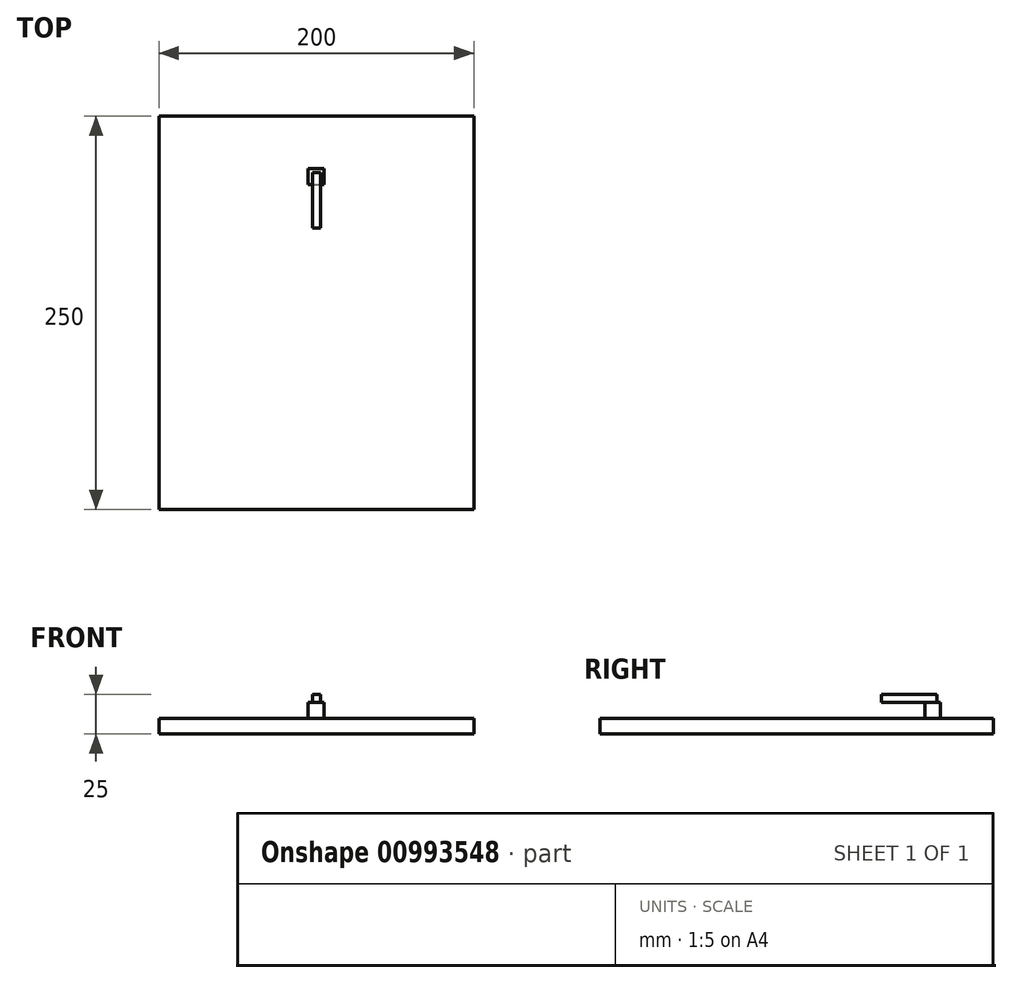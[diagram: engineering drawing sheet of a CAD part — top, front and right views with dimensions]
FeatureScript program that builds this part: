
annotation { "Feature Type Name" : "Feature", "Feature Type Description" : "" }
export const myFeature = defineFeature(function(context is Context, id is Id, definition is map)
    precondition{}
    {
        {
            var Q0;
            Q0=qCreatedBy(makeId("Top.planeOp"),FACE);
            var sketch = newSketch(context, id + "F0", { "sketchPlane" : qUnion([Q0])});
            skLineSegment(sketch, "E0.bottom", {"start": v(100, -125) * mm, "end": v(-100, -125) * mm});
            skLineSegment(sketch, "E0.top", {"start": v(100, 125) * mm, "end": v(-100, 125) * mm});
            skLineSegment(sketch, "E0.left", {"start": v(100, -125) * mm, "end": v(100, 125) * mm});
            skLineSegment(sketch, "E0.right", {"start": v(-100, -125) * mm, "end": v(-100, 125) * mm});
            skPoint(sketch, "E0.middle", {"position": v(0, 0) * mm});
            skSolve(sketch);
        }
        {
            var Q0;
            Q0 = qSketchRegion(id + "F0", true);
            extrude(context, id + "F1", {"entities" : qUnion([Q0]), "depth" : 10 * mm, "offsetDistance" : 25 * mm});
        }
        {
            var Q0;
            Q0=makeQuery(id+"F1.opExtrude","CAP_FACE",FACE,{"disambiguationData":[OSD([sQuery(id+"F0.wireOp",EDGE,"E0.bottom"),sQuery(id+"F0.wireOp",EDGE,"E0.top"),sQuery(id+"F0.wireOp",EDGE,"E0.left"),sQuery(id+"F0.wireOp",EDGE,"E0.right")])],"isStart":false});
            var sketch = newSketch(context, id + "F2", { "sketchPlane" : qUnion([Q0])});
            skLineSegment(sketch, "E1.bottom", {"start": v(-5.22, 91.46) * mm, "end": v(4.78, 91.46) * mm});
            skLineSegment(sketch, "E1.top", {"start": v(-5.22, 81.46) * mm, "end": v(4.78, 81.46) * mm});
            skLineSegment(sketch, "E1.left", {"start": v(-5.22, 91.46) * mm, "end": v(-5.22, 81.46) * mm});
            skLineSegment(sketch, "E1.right", {"start": v(4.78, 91.46) * mm, "end": v(4.78, 81.46) * mm});
            skLineSegment(sketch, "E2", {"start": v(0, 0) * mm, "end": v(0, 120.17) * mm});
            skSolve(sketch);
        }
        {
            var Q0;
            Q0 = qSketchRegion(id + "F2", true);
            extrude(context, id + "F3", {"entities" : qUnion([Q0]), "operationType" : NewBodyOperationType.ADD, "depth" : 10 * mm, "offsetDistance" : 25 * mm});
        }
        {
            var Q0;
            Q0=qCreatedBy(makeId("Top.planeOp"),FACE);
            cPlane(context, id + "F4", {"entities" : qUnion([Q0]), "cplaneType" : CPlaneType.OFFSET, "offset" : 20.1 * mm, "width" : 150 * mm, "height" : 150 * mm});
        }
        {
            var Q0;
            Q0=makeQuery(id+"F3.opExtrude","CAP_FACE",FACE,{"disambiguationData":[OSD([sQuery(id+"F2.wireOp",EDGE,"E1.bottom"),sQuery(id+"F2.wireOp",EDGE,"E1.top"),sQuery(id+"F2.wireOp",EDGE,"E1.left"),sQuery(id+"F2.wireOp",EDGE,"E1.right")])],"isStart":false});
            var sketch = newSketch(context, id + "F5", { "sketchPlane" : qUnion([Q0])});
            skLineSegment(sketch, "E3.bottom", {"start": v(2.6, 83.82) * mm, "end": v(-2.6, 83.82) * mm});
            skLineSegment(sketch, "E3.top", {"start": v(2.6, 88.96) * mm, "end": v(-2.6, 88.96) * mm});
            skLineSegment(sketch, "E3.left", {"start": v(2.6, 83.82) * mm, "end": v(2.6, 88.96) * mm});
            skLineSegment(sketch, "E3.right", {"start": v(-2.6, 83.82) * mm, "end": v(-2.6, 88.96) * mm});
            skPoint(sketch, "E3.middle", {"position": v(0, 86.4) * mm});
            skSolve(sketch);
        }
        {
            var Q0;
            Q0=makeQuery(id+"F5.imprint","IMPRINT",FACE,{"disambiguationData":[TD([[makeQuery(id+"F5.imprint","IMPRINT",EDGE,{"derivedFrom":sQuery(id+"F5.wireOp",EDGE,"E3.bottom")}),-1.0]])]});
            extrude(context, id + "F6", {"entities" : qUnion([Q0]), "operationType" : NewBodyOperationType.ADD, "depth" : 5 * mm, "offsetDistance" : 25 * mm});
        }
        {
            var Q0;
            Q0=makeQuery(id+"F6.opExtrude","SWEPT_FACE",FACE,{"disambiguationData":[OSD([sQuery(id+"F5.wireOp",EDGE,"E3.bottom")])]});
            var sketch = newSketch(context, id + "F7", { "sketchPlane" : qUnion([Q0])});
            skLineSegment(sketch, "E4.bottom", {"start": v(-2.6, 25) * mm, "end": v(2.6, 25) * mm});
            skLineSegment(sketch, "E4.top", {"start": v(-2.6, 20) * mm, "end": v(2.6, 20) * mm});
            skLineSegment(sketch, "E4.left", {"start": v(-2.6, 25) * mm, "end": v(-2.6, 20) * mm});
            skLineSegment(sketch, "E4.right", {"start": v(2.6, 25) * mm, "end": v(2.6, 20) * mm});
            skSolve(sketch);
        }
        {
            var Q0;
            Q0 = qSketchRegion(id + "F7", true);
            extrude(context, id + "F8", {"entities" : qUnion([Q0]), "operationType" : NewBodyOperationType.ADD, "depth" : 30 * mm, "offsetDistance" : 25 * mm});
        }
    });
